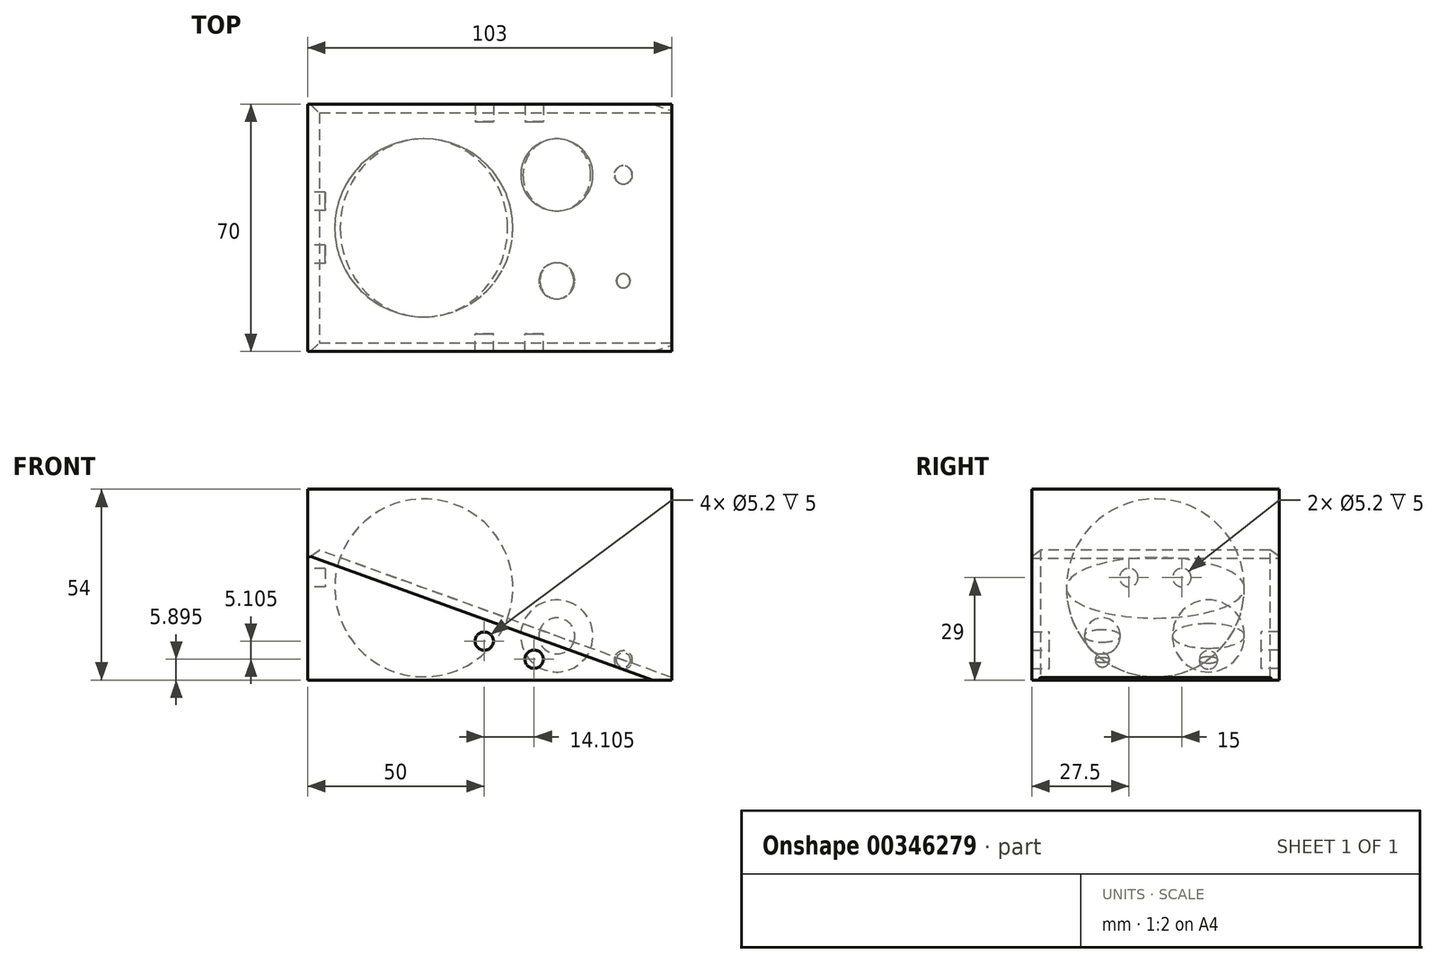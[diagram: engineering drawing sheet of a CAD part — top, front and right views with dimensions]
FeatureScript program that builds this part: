
annotation { "Feature Type Name" : "Feature", "Feature Type Description" : "" }
export const myFeature = defineFeature(function(context is Context, id is Id, definition is map)
    precondition{}
    {
        {
            var Q0;
            Q0=qCreatedBy(makeId("Front.planeOp"),FACE);
            var sketch = newSketch(context, id + "F0", { "sketchPlane" : qUnion([Q0])});
            skLineSegment(sketch, "E0", {"start": v(0, 0) * mm, "end": v(105, 0) * mm});
            skLineSegment(sketch, "E1", {"start": v(0, 38) * mm, "end": v(0, 0) * mm});
            skLineSegment(sketch, "E2", {"start": v(0, 38) * mm, "end": v(105, 0) * mm});
            skLineSegment(sketch, "E3", {"start": v(103, 0.72) * mm, "end": v(103, 0) * mm});
            skSolve(sketch);
        }
        {
            var Q0;
            {var subQ0=sQuery(id+"F0.wireOp",EDGE,"bQABj8yy-q7AW-h4jb-vGEl-2AM3qVuoejDB");Q0=makeQuery(id+"F0.imprint","IMPRINT",FACE,{"disambiguationData":[TD([[makeQuery(id+"F0.imprint","IMPRINT",EDGE,{"derivedFrom":subQ0}),-1.0]])]});}
            var Q1;
            {var subQ0=sQuery(id+"F0.wireOp",EDGE,"JrbFQyJT-Unaw-xspN-WVzr-I55S5pEqG3a4");Q1=makeQuery(id+"F0.imprint","IMPRINT",FACE,{"disambiguationData":[TD([[makeQuery(id+"F0.imprint","IMPRINT",EDGE,{"derivedFrom":subQ0}),-1.0]])]});}
            var Q2;
            {var subQ1=sQuery(id+"F0.wireOp",EDGE,"FhE3cFBd-a02A-WwM5-fFk2-cJB4Byv2OZIA");Q2=makeQuery(id+"F0.imprint","IMPRINT",FACE,{"disambiguationData":[TD([[makeQuery(id+"F0.imprint","IMPRINT",EDGE,{"derivedFrom":subQ1}),-1.0]])]});}
            var Q3;
            {var subQ0=sQuery(id+"F0.wireOp",EDGE,"U0bc4D1h-haUk-CMOQ-H1PB-d3JZDOPnEGFL");Q3=makeQuery(id+"F0.imprint","IMPRINT",FACE,{"disambiguationData":[TD([[makeQuery(id+"F0.imprint","IMPRINT",EDGE,{"derivedFrom":subQ0}),-1.0]])]});}
            var Q4;
            {var subQ0=sQuery(id+"F0.wireOp",EDGE,"Cph3fWDO-xWAI-Ux1v-VPcS-VOfUcQn6UrrE");Q4=makeQuery(id+"F0.imprint","IMPRINT",FACE,{"disambiguationData":[TD([[makeQuery(id+"F0.imprint","IMPRINT",EDGE,{"derivedFrom":subQ0}),-1.0]])]});}
            var Q5;
            {var subQ0=sQuery(id+"F0.wireOp",EDGE,"E1");Q5=makeQuery(id+"F0.imprint","IMPRINT",FACE,{"disambiguationData":[TD([[makeQuery(id+"F0.imprint","IMPRINT",EDGE,{"derivedFrom":subQ0}),1.0]])]});}
            extrude(context, id + "F1", {"entities" : qUnion([Q0, Q1, Q2, Q3, Q4, Q5]), "depth" : 35 * mm, "hasSecondDirection" : true, "secondDirectionOppositeDirection" : true, "secondDirectionDepth" : 35 * mm});
        }
        {
            var Q0;
            Q0=makeQuery(id+"F1.opExtrude","SWEPT_FACE",FACE,{"disambiguationData":[OSD([sQuery(id+"F0.wireOp",EDGE,"E2")])]});
            cPlane(context, id + "F2", {"entities" : qUnion([Q0]), "cplaneType" : CPlaneType.OFFSET, "offset" : 0 * mm, "width" : 150 * mm, "height" : 150 * mm});
        }
        {
            var Q0;
            Q0=qCreatedBy(id+"F2.planeOp",FACE);
            var sketch = newSketch(context, id + "F3", { "sketchPlane" : qUnion([Q0])});
            skPoint(sketch, "E4", {"position": v(-12.93, 0) * mm});
            skPoint(sketch, "E5", {"position": v(0, 0) * mm});
            skLineSegment(sketch, "E6", {"start": v(-12.93, 0) * mm, "end": v(0, 0) * mm, "construction": true});
            skCircle(sketch, "E7", {"center": v(22.07, 0) * mm, "radius": 25.2 * mm});
            skCircle(sketch, "E8", {"center": v(62.07, -15) * mm, "radius": 5.1 * mm});
            skCircle(sketch, "E9", {"center": v(62.07, 15) * mm, "radius": 10.2 * mm});
            skCircle(sketch, "E10", {"center": v(82.07, 15) * mm, "radius": 2.6 * mm});
            skCircle(sketch, "E11", {"center": v(82.07, -15) * mm, "radius": 2 * mm});
            skLineSegment(sketch, "E12", {"start": v(62.07, -15) * mm, "end": v(67.17, -15) * mm});
            skLineSegment(sketch, "E13", {"start": v(62.07, -15) * mm, "end": v(56.97, -15) * mm});
            skLineSegment(sketch, "E14", {"start": v(62.07, 15) * mm, "end": v(51.87, 15) * mm});
            skLineSegment(sketch, "E15", {"start": v(62.07, 15) * mm, "end": v(72.27, 15) * mm});
            skLineSegment(sketch, "E16", {"start": v(82.07, -15) * mm, "end": v(80.07, -15) * mm});
            skLineSegment(sketch, "E17", {"start": v(82.07, -15) * mm, "end": v(84.07, -15) * mm});
            skLineSegment(sketch, "E18", {"start": v(82.07, 15) * mm, "end": v(79.47, 15) * mm});
            skLineSegment(sketch, "E19", {"start": v(82.07, 15) * mm, "end": v(84.67, 15) * mm});
            skLineSegment(sketch, "E20", {"start": v(-3.13, 0) * mm, "end": v(47.27, 0) * mm});
            skSolve(sketch);
        }
        {
            var Q0;
            {var subQ0=sQuery(id+"F3.wireOp",EDGE,"E20");Q0=makeQuery(id+"F3.imprint","IMPRINT",FACE,{"disambiguationData":[TD([[makeQuery(id+"F3.imprint","IMPRINT",EDGE,{"derivedFrom":subQ0}),-1.0]])]});}
            var Q1;
            Q1=sQuery(id+"F3.wireOp",EDGE,"E20");
            revolve(context, id + "F4", {"operationType" : NewBodyOperationType.REMOVE, "entities" : qUnion([Q0]), "axis" : qUnion([Q1]), "revolveType" : RevolveType.FULL, "oppositeDirection" : true});
        }
        {
            var Q0;
            {var subQ0=sQuery(id+"F3.wireOp",EDGE,"E12");Q0=makeQuery(id+"F3.imprint","IMPRINT",FACE,{"disambiguationData":[TD([[makeQuery(id+"F3.imprint","IMPRINT",EDGE,{"derivedFrom":subQ0}),-1.0]])]});}
            var Q1;
            Q1=sQuery(id+"F3.wireOp",EDGE,"E13");
            revolve(context, id + "F5", {"operationType" : NewBodyOperationType.REMOVE, "entities" : qUnion([Q0]), "axis" : qUnion([Q1]), "revolveType" : RevolveType.FULL, "oppositeDirection" : true});
        }
        {
            var Q0;
            {var subQ0=sQuery(id+"F3.wireOp",EDGE,"E14");Q0=makeQuery(id+"F3.imprint","IMPRINT",FACE,{"disambiguationData":[TD([[makeQuery(id+"F3.imprint","IMPRINT",EDGE,{"derivedFrom":subQ0}),1.0]])]});}
            var Q1;
            Q1=sQuery(id+"F3.wireOp",EDGE,"E14");
            revolve(context, id + "F6", {"operationType" : NewBodyOperationType.REMOVE, "entities" : qUnion([Q0]), "axis" : qUnion([Q1]), "revolveType" : RevolveType.FULL, "oppositeDirection" : true});
        }
        {
            var Q0;
            {var subQ0=sQuery(id+"F3.wireOp",EDGE,"E16");Q0=makeQuery(id+"F3.imprint","IMPRINT",FACE,{"disambiguationData":[TD([[makeQuery(id+"F3.imprint","IMPRINT",EDGE,{"derivedFrom":subQ0}),1.0]])]});}
            var Q1;
            Q1=sQuery(id+"F3.wireOp",EDGE,"E16");
            revolve(context, id + "F7", {"operationType" : NewBodyOperationType.REMOVE, "entities" : qUnion([Q0]), "axis" : qUnion([Q1]), "revolveType" : RevolveType.FULL, "oppositeDirection" : true});
        }
        {
            var Q0;
            {var subQ0=sQuery(id+"F3.wireOp",EDGE,"E18");Q0=makeQuery(id+"F3.imprint","IMPRINT",FACE,{"disambiguationData":[TD([[makeQuery(id+"F3.imprint","IMPRINT",EDGE,{"derivedFrom":subQ0}),1.0]])]});}
            var Q1;
            Q1=sQuery(id+"F3.wireOp",EDGE,"E18");
            revolve(context, id + "F8", {"operationType" : NewBodyOperationType.REMOVE, "entities" : qUnion([Q0]), "axis" : qUnion([Q1]), "revolveType" : RevolveType.FULL, "oppositeDirection" : true});
        }
        {
            var Q0;
            {var subQ0=sQuery(id+"F3.wireOp",EDGE,"E20");Q0=makeQuery(id+"F3.imprint","IMPRINT",FACE,{"disambiguationData":[TD([[makeQuery(id+"F3.imprint","IMPRINT",EDGE,{"derivedFrom":subQ0}),-1.0]])]});}
            var Q1;
            Q1=sQuery(id+"F3.wireOp",EDGE,"E20");
            revolve(context, id + "F9", {"entities" : qUnion([Q0]), "axis" : qUnion([Q1]), "revolveType" : RevolveType.FULL});
        }
        {
            var Q0;
            {var subQ0=sQuery(id+"F3.wireOp",EDGE,"E14");Q0=makeQuery(id+"F3.imprint","IMPRINT",FACE,{"disambiguationData":[TD([[makeQuery(id+"F3.imprint","IMPRINT",EDGE,{"derivedFrom":subQ0}),1.0]])]});}
            var Q1;
            Q1=sQuery(id+"F3.wireOp",EDGE,"E14");
            revolve(context, id + "F10", {"entities" : qUnion([Q0]), "axis" : qUnion([Q1]), "revolveType" : RevolveType.FULL});
        }
        {
            var Q0;
            {var subQ0=sQuery(id+"F3.wireOp",EDGE,"E12");Q0=makeQuery(id+"F3.imprint","IMPRINT",FACE,{"disambiguationData":[TD([[makeQuery(id+"F3.imprint","IMPRINT",EDGE,{"derivedFrom":subQ0}),-1.0]])]});}
            var Q1;
            Q1=sQuery(id+"F3.wireOp",EDGE,"E13");
            revolve(context, id + "F11", {"entities" : qUnion([Q0]), "axis" : qUnion([Q1]), "revolveType" : RevolveType.FULL});
        }
        {
            var Q0;
            {var subQ0=sQuery(id+"F3.wireOp",EDGE,"E18");Q0=makeQuery(id+"F3.imprint","IMPRINT",FACE,{"disambiguationData":[TD([[makeQuery(id+"F3.imprint","IMPRINT",EDGE,{"derivedFrom":subQ0}),1.0]])]});}
            var Q1;
            Q1=sQuery(id+"F3.wireOp",EDGE,"E18");
            revolve(context, id + "F12", {"entities" : qUnion([Q0]), "axis" : qUnion([Q1]), "revolveType" : RevolveType.FULL});
        }
        {
            var Q0;
            {var subQ0=sQuery(id+"F3.wireOp",EDGE,"E16");Q0=makeQuery(id+"F3.imprint","IMPRINT",FACE,{"disambiguationData":[TD([[makeQuery(id+"F3.imprint","IMPRINT",EDGE,{"derivedFrom":subQ0}),1.0]])]});}
            var Q1;
            Q1=sQuery(id+"F3.wireOp",EDGE,"E16");
            revolve(context, id + "F13", {"entities" : qUnion([Q0]), "axis" : qUnion([Q1]), "revolveType" : RevolveType.FULL});
        }
        {
            var Q0;
            Q0=qCreatedBy(makeId("Top.planeOp"),FACE);
            var sketch = newSketch(context, id + "F14", { "sketchPlane" : qUnion([Q0])});
            skLineSegment(sketch, "E21.bottom", {"start": v(0, -35) * mm, "end": v(103, -35) * mm});
            skLineSegment(sketch, "E21.top", {"start": v(0, 35) * mm, "end": v(103, 35) * mm});
            skLineSegment(sketch, "E21.left", {"start": v(0, -35) * mm, "end": v(0, 35) * mm});
            skLineSegment(sketch, "E21.right", {"start": v(103, -35) * mm, "end": v(103, 35) * mm});
            skSolve(sketch);
        }
        {
            var Q0;
            Q0 = qSketchRegion(id + "F14", true);
            extrude(context, id + "F15", {"entities" : qUnion([Q0]), "depth" : 54 * mm});
        }
        {
            var Q0;
            Q0=makeQuery(id+"F1.opExtrude","CAP_EDGE",EDGE,{"disambiguationData":[OSD([sQuery(id+"F0.wireOp",EDGE,"E2")])],"isStart":false});
            var Q1;
            Q1=makeQuery(id+"F1.opExtrude","SWEPT_EDGE",EDGE,{"disambiguationData":[OSD([sQuery(id+"F0.wireOp",EDGE,"E1"),sQuery(id+"F0.wireOp",EDGE,"E2")])]});
            var Q2;
            Q2=makeQuery(id+"F1.opExtrude","CAP_EDGE",EDGE,{"disambiguationData":[OSD([sQuery(id+"F0.wireOp",EDGE,"E2")])],"isStart":true});
            chamfer(context, id + "F16", {"entities" : qUnion([Q0, Q1, Q2]), "width" : 2.5 * mm, "tangentPropagation" : true});
        }
        {
            var Q0;
            Q0=makeQuery(id+"F13.opRevolve","SWEPT_BODY",BODY,{"disambiguationData":[OSD([sQuery(id+"F3.wireOp",EDGE,"E11"),sQuery(id+"F3.wireOp",EDGE,"E16"),sQuery(id+"F3.wireOp",EDGE,"E17")])]});
            var Q1;
            Q1=makeQuery(id+"F12.opRevolve","SWEPT_BODY",BODY,{"disambiguationData":[OSD([sQuery(id+"F3.wireOp",EDGE,"E10"),sQuery(id+"F3.wireOp",EDGE,"E18"),sQuery(id+"F3.wireOp",EDGE,"E19")])]});
            var Q2;
            Q2=makeQuery(id+"F11.opRevolve","SWEPT_BODY",BODY,{"disambiguationData":[OSD([sQuery(id+"F3.wireOp",EDGE,"E8"),sQuery(id+"F3.wireOp",EDGE,"E12"),sQuery(id+"F3.wireOp",EDGE,"E13")])]});
            var Q3;
            Q3=makeQuery(id+"F10.opRevolve","SWEPT_BODY",BODY,{"disambiguationData":[OSD([sQuery(id+"F3.wireOp",EDGE,"E9"),sQuery(id+"F3.wireOp",EDGE,"E14"),sQuery(id+"F3.wireOp",EDGE,"E15")])]});
            var Q4;
            Q4=makeQuery(id+"F9.opRevolve","SWEPT_BODY",BODY,{"disambiguationData":[OSD([sQuery(id+"F3.wireOp",EDGE,"E7"),sQuery(id+"F3.wireOp",EDGE,"E20")])]});
            var Q5;
            Q5=makeQuery(id+"F1.opExtrude","SWEPT_BODY",BODY,{"disambiguationData":[OSD([sQuery(id+"F0.wireOp",EDGE,"E0"),sQuery(id+"F0.wireOp",EDGE,"E1"),sQuery(id+"F0.wireOp",EDGE,"E2"),sQuery(id+"F0.wireOp",EDGE,"E3")])]});
            var Q6;
            Q6=makeQuery(id+"F15.opExtrude","SWEPT_BODY",BODY,{"disambiguationData":[OSD([sQuery(id+"F14.wireOp",EDGE,"E21.bottom"),sQuery(id+"F14.wireOp",EDGE,"E21.top"),sQuery(id+"F14.wireOp",EDGE,"E21.left"),sQuery(id+"F14.wireOp",EDGE,"E21.right")])]});
            booleanBodies(context, id + "F17", {"operationType" : BooleanOperationType.SUBTRACTION, "tools" : qUnion([Q0, Q1, Q2, Q3, Q4, Q5]), "targets" : qUnion([Q6]), "keepTools" : true});
        }
        {
            var Q0;
            Q0=qCreatedBy(makeId("Front.planeOp"),FACE);
            var sketch = newSketch(context, id + "F18", { "sketchPlane" : qUnion([Q0])});
            skCircle(sketch, "E22", {"center": v(50, 11) * mm, "radius": 2.6 * mm});
            skCircle(sketch, "E23", {"center": v(64.1, 5.9) * mm, "radius": 2.6 * mm});
            skLineSegment(sketch, "E24", {"start": v(50, 11) * mm, "end": v(64.1, 5.9) * mm});
            skSolve(sketch);
        }
        {
            var Q0;
            Q0 = qSketchRegion(id + "F18", true);
            var Q1;
            Q1=makeQuery(id+"F1.opExtrude","CAP_FACE",FACE,{"disambiguationData":[OSD([sQuery(id+"F0.wireOp",EDGE,"E0"),sQuery(id+"F0.wireOp",EDGE,"E1"),sQuery(id+"F0.wireOp",EDGE,"E2"),sQuery(id+"F0.wireOp",EDGE,"E3")])],"isStart":false});
            extrude(context, id + "F19", {"entities" : qUnion([Q0]), "operationType" : NewBodyOperationType.REMOVE, "endBound" : BoundingType.UP_TO_SURFACE, "endBoundEntityFace" : qUnion([Q1]), "depth" : 25 * mm, "hasSecondDirection" : true, "secondDirectionOppositeDirection" : false, "secondDirectionDepth" : 30 * mm});
        }
        {
            var Q0;
            Q0 = qSketchRegion(id + "F18", true);
            var Q1;
            Q1=makeQuery(id+"F1.opExtrude","CAP_FACE",FACE,{"disambiguationData":[OSD([sQuery(id+"F0.wireOp",EDGE,"E0"),sQuery(id+"F0.wireOp",EDGE,"E1"),sQuery(id+"F0.wireOp",EDGE,"E2"),sQuery(id+"F0.wireOp",EDGE,"E3")])],"isStart":true});
            extrude(context, id + "F20", {"entities" : qUnion([Q0]), "operationType" : NewBodyOperationType.REMOVE, "endBound" : BoundingType.UP_TO_SURFACE, "oppositeDirection" : true, "endBoundEntityFace" : qUnion([Q1]), "depth" : 25 * mm, "hasSecondDirection" : true, "secondDirectionOppositeDirection" : true, "secondDirectionDepth" : 30 * mm});
        }
        {
            var Q0;
            Q0=makeQuery(id+"F1.opExtrude","SWEPT_FACE",FACE,{"disambiguationData":[OSD([sQuery(id+"F0.wireOp",EDGE,"E1")])]});
            var sketch = newSketch(context, id + "F21", { "sketchPlane" : qUnion([Q0])});
            skCircle(sketch, "E25", {"center": v(-7.5, 29) * mm, "radius": 2.6 * mm});
            skCircle(sketch, "E26", {"center": v(7.5, 29) * mm, "radius": 2.6 * mm});
            skLineSegment(sketch, "E27", {"start": v(-7.5, 29) * mm, "end": v(7.5, 29) * mm, "construction": true});
            skLineSegment(sketch, "E28", {"start": v(0, 29) * mm, "end": v(0, 0) * mm, "construction": true});
            skSolve(sketch);
        }
        {
            var Q0;
            Q0 = qSketchRegion(id + "F21", true);
            extrude(context, id + "F22", {"entities" : qUnion([Q0]), "operationType" : NewBodyOperationType.REMOVE, "oppositeDirection" : true, "depth" : 5 * mm});
        }
    });
